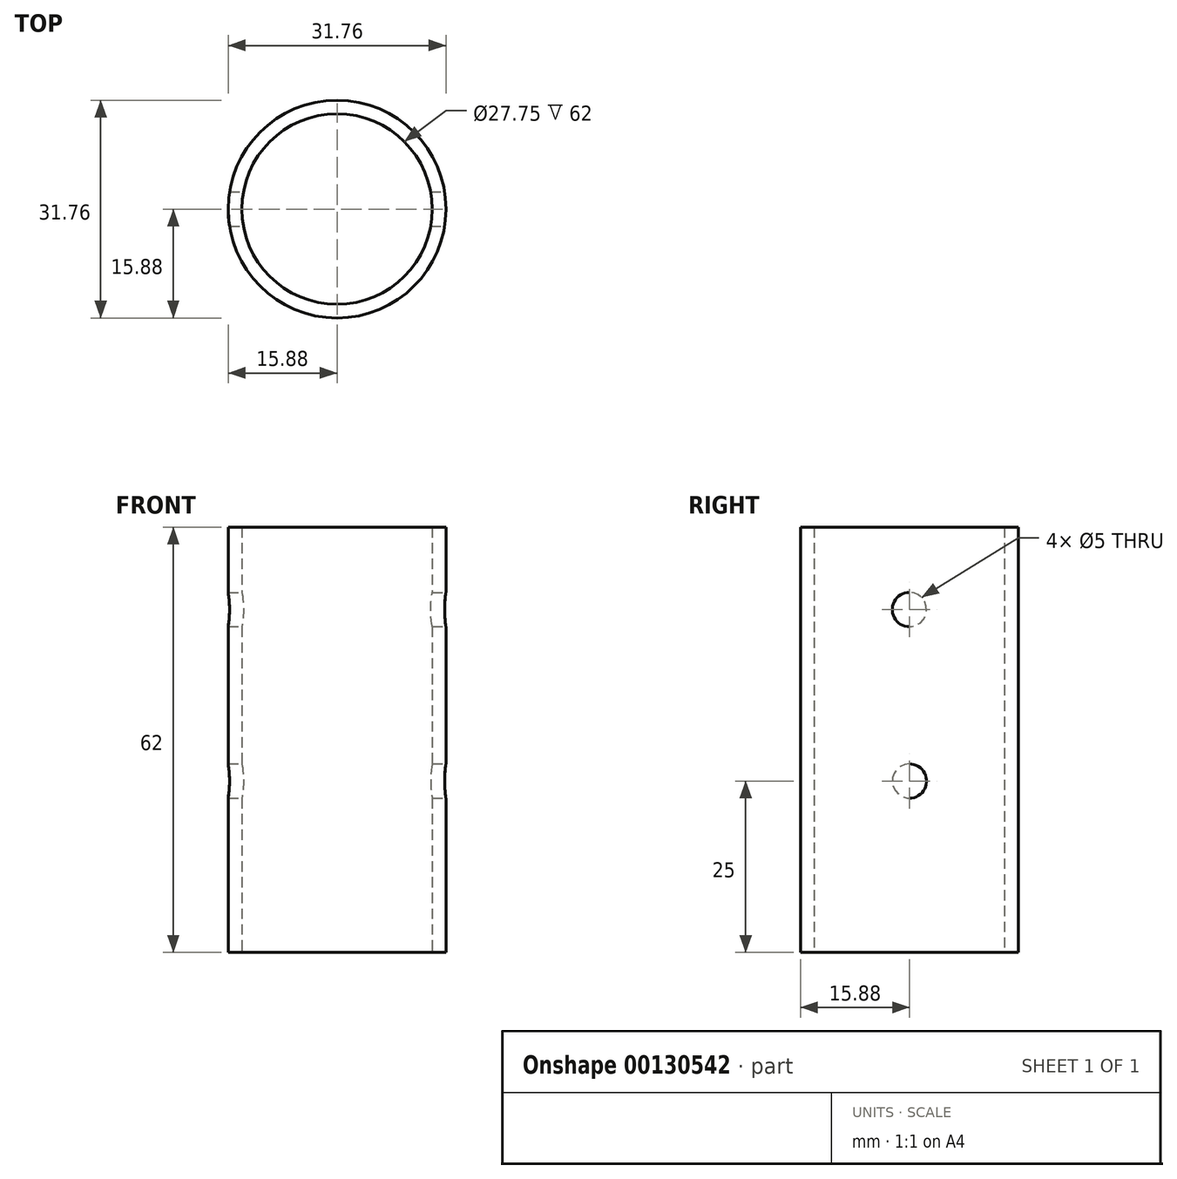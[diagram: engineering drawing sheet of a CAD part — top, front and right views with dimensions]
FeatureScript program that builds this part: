
annotation { "Feature Type Name" : "Feature", "Feature Type Description" : "" }
export const myFeature = defineFeature(function(context is Context, id is Id, definition is map)
    precondition{}
    {
        {
            var Q0;
            Q0=qCreatedBy(makeId("Top.planeOp"),FACE);
            var sketch = newSketch(context, id + "F0", { "sketchPlane" : qUnion([Q0])});
            skCircle(sketch, "E0", {"center": v(0, 0) * mm, "radius": 13.88 * mm});
            skCircle(sketch, "E1.0", {"center": v(0, 0) * mm, "radius": 15.88 * mm});
            skSolve(sketch);
        }
        {
            var Q0;
            Q0=makeQuery(id+"F0.imprint","IMPRINT",FACE,{"disambiguationData":[TD([[makeQuery(id+"F0.imprint","IMPRINT",EDGE,{"derivedFrom":sQuery(id+"F0.wireOp",EDGE,"E0")}),-1.0]])]});
            extrude(context, id + "F1", {"entities" : qUnion([Q0]), "depth" : 62 * mm});
        }
        {
            var Q0;
            Q0=qCreatedBy(makeId("Right.planeOp"),FACE);
            var sketch = newSketch(context, id + "F2", { "sketchPlane" : qUnion([Q0])});
            skCircle(sketch, "E2", {"center": v(0, 50) * mm, "radius": 2.5 * mm});
            skCircle(sketch, "E3", {"center": v(0, 25) * mm, "radius": 2.5 * mm});
            skSolve(sketch);
        }
        {
            var Q0;
            Q0 = qSketchRegion(id + "F2", true);
            extrude(context, id + "F3", {"entities" : qUnion([Q0]), "operationType" : NewBodyOperationType.REMOVE, "oppositeDirection" : true, "depth" : 50 * mm, "symmetric" : true});
        }
    });
